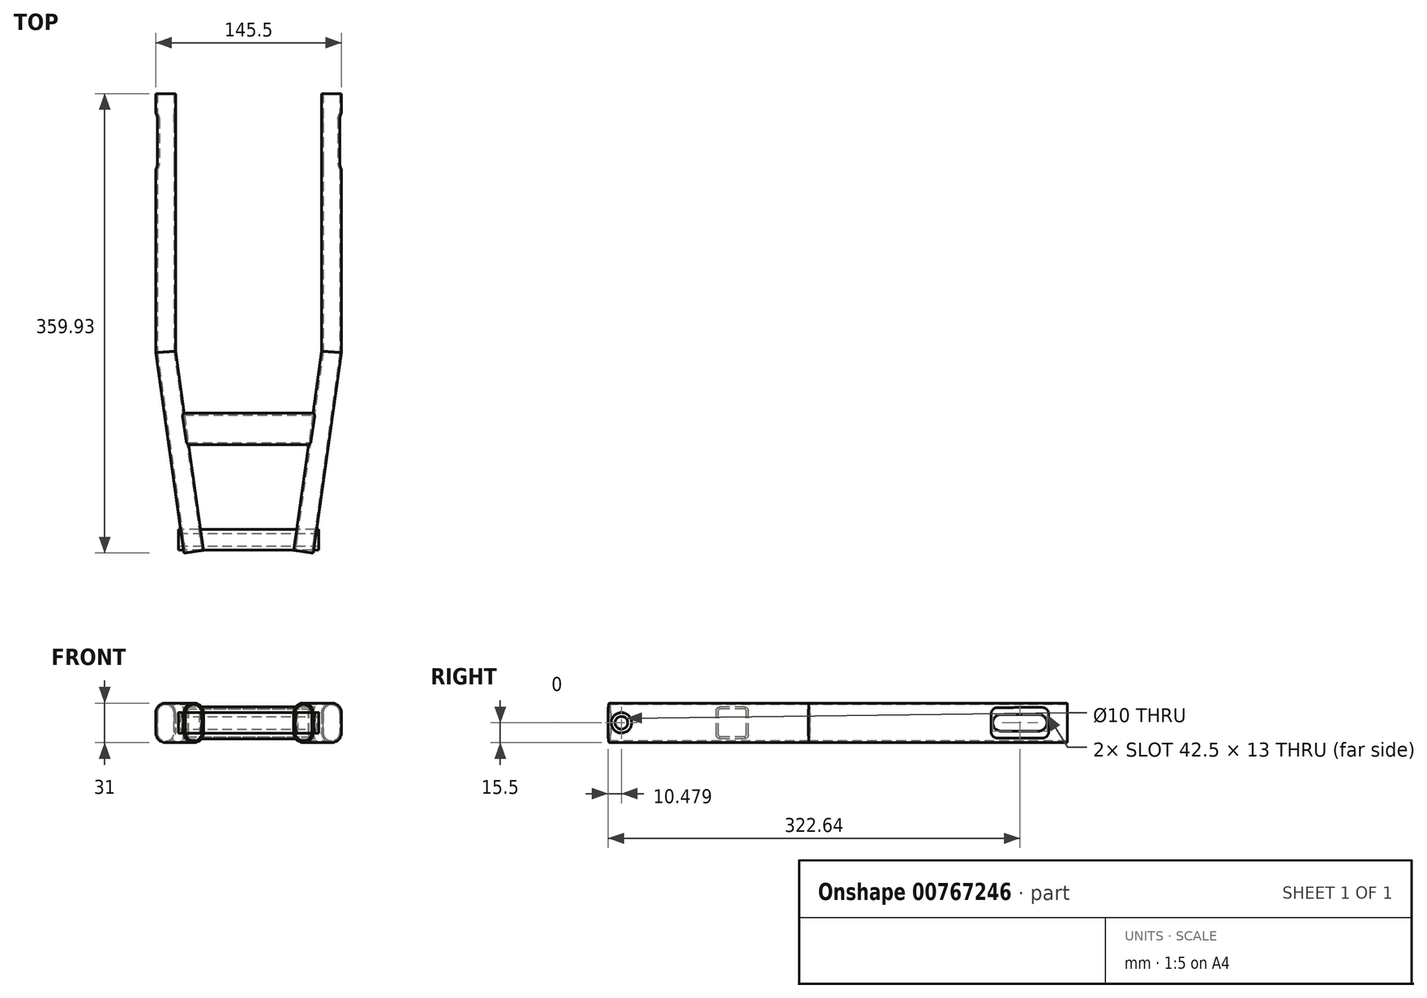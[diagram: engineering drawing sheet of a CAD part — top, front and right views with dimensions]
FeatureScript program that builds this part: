
annotation { "Feature Type Name" : "Feature", "Feature Type Description" : "" }
export const myFeature = defineFeature(function(context is Context, id is Id, definition is map)
    precondition{}
    {
        {
            var Q0;
            Q0=qCreatedBy(makeId("Top.planeOp"),FACE);
            var sketch = newSketch(context, id + "F0", { "sketchPlane" : qUnion([Q0])});
            skLineSegment(sketch, "E0", {"start": v(-65, 0) * mm, "end": v(-65, -202.36) * mm});
            skLineSegment(sketch, "E1", {"start": v(-65, -202.36) * mm, "end": v(-43, -358.85) * mm});
            skSolve(sketch);
        }
        {
            var Q0;
            Q0=qCreatedBy(makeId("Front.planeOp"),FACE);
            var sketch = newSketch(context, id + "F1", { "sketchPlane" : qUnion([Q0])});
            skLineSegment(sketch, "E2.left", {"start": v(-72.75, 7.75) * mm, "end": v(-72.75, -7.75) * mm});
            skLineSegment(sketch, "E2.right", {"start": v(-57.25, 7.75) * mm, "end": v(-57.25, -7.75) * mm});
            skPoint(sketch, "E2.middle", {"position": v(-65, 0) * mm});
            skArc(sketch, "E3", {"start": v(-57.25, 7.75) * mm, "mid": v(-65, 15.5) * mm, "end": v(-72.75, 7.75) * mm});
            skArc(sketch, "E4", {"start": v(-57.25, -7.75) * mm, "mid": v(-65, -15.5) * mm, "end": v(-72.75, -7.75) * mm});
            skPoint(sketch, "E5.left.start.orphan", {"position": v(-71.55, 6.63) * mm});
            skPoint(sketch, "E5.top.start.orphan", {"position": v(-71.55, -6.63) * mm});
            skPoint(sketch, "E5.right.end.orphan", {"position": v(-58.45, -6.63) * mm});
            skPoint(sketch, "E5.right.start.orphan", {"position": v(-58.45, 6.63) * mm});
            skArc(sketch, "E6.0", {"start": v(-58.45, 7.75) * mm, "mid": v(-65, 14.3) * mm, "end": v(-71.55, 7.75) * mm});
            skLineSegment(sketch, "E6.1", {"start": v(-58.45, 7.75) * mm, "end": v(-58.45, -7.75) * mm});
            skArc(sketch, "E6.2", {"start": v(-58.45, -7.75) * mm, "mid": v(-65, -14.3) * mm, "end": v(-71.55, -7.75) * mm});
            skLineSegment(sketch, "E6.3", {"start": v(-71.55, 7.75) * mm, "end": v(-71.55, -7.75) * mm});
            skSolve(sketch);
        }
        {
            var Q0;
            Q0=makeQuery(id+"F1.imprint","IMPRINT",FACE,{"disambiguationData":[TD([[makeQuery(id+"F1.imprint","IMPRINT",EDGE,{"derivedFrom":sQuery(id+"F1.wireOp",EDGE,"E2.left")}),1.0]])]});
            var Q1;
            Q1=sQuery(id+"F0.wireOp",EDGE,"E0");
            var Q2;
            Q2=sQuery(id+"F0.wireOp",EDGE,"E1");
            sweep(context, id + "F2", {"profiles" : qUnion([Q0]), "path" : qUnion([Q1, Q2])});
        }
        {
            var Q0;
            Q0=makeQuery(id+"F2.opSweep","SWEPT_BODY",BODY,{"disambiguationData":[OSD([sQuery(id+"F0.wireOp",EDGE,"E1"),sQuery(id+"F1.wireOp",EDGE,"E2.left"),sQuery(id+"F1.wireOp",EDGE,"E2.right"),sQuery(id+"F1.wireOp",EDGE,"E3"),sQuery(id+"F1.wireOp",EDGE,"E4"),sQuery(id+"F1.wireOp",EDGE,"E6.0"),sQuery(id+"F1.wireOp",EDGE,"E6.1"),sQuery(id+"F1.wireOp",EDGE,"E6.2"),sQuery(id+"F1.wireOp",EDGE,"E6.3")])]});
            var Q1;
            Q1=qCreatedBy(makeId("Right.planeOp"),FACE);
            mirror(context, id + "F3", {"entities" : qUnion([Q0]), "mirrorPlane" : qUnion([Q1])});
        }
        {
            var Q0;
            Q0=qCreatedBy(makeId("Right.planeOp"),FACE);
            var sketch = newSketch(context, id + "F4", { "sketchPlane" : qUnion([Q0])});
            skLineSegment(sketch, "E7.bottom", {"start": v(-52.04, 6.5) * mm, "end": v(-22.54, 6.5) * mm});
            skLineSegment(sketch, "E7.top", {"start": v(-52.04, -6.5) * mm, "end": v(-22.54, -6.5) * mm});
            skLineSegment(sketch, "E7.left", {"start": v(-52.04, 6.5) * mm, "end": v(-52.04, -6.5) * mm});
            skLineSegment(sketch, "E7.right", {"start": v(-22.54, 6.5) * mm, "end": v(-22.54, -6.5) * mm});
            skPoint(sketch, "E7.middle", {"position": v(-37.3, 0) * mm});
            skArc(sketch, "E8", {"start": v(-22.54, 6.5) * mm, "mid": v(-16.04, 0) * mm, "end": v(-22.54, -6.5) * mm});
            skArc(sketch, "E9", {"start": v(-52.04, 6.5) * mm, "mid": v(-58.54, 0) * mm, "end": v(-52.04, -6.5) * mm});
            skSolve(sketch);
        }
        {
            var Q0;
            Q0 = qSketchRegion(id + "F4", true);
            extrude(context, id + "F5", {"entities" : qUnion([Q0]), "operationType" : NewBodyOperationType.REMOVE, "endBound" : BoundingType.SYMMETRIC, "oppositeDirection" : true, "depth" : 1000 * mm, "offsetDistance" : 25 * mm});
        }
        {
            var Q0;
            Q0=makeQuery(id+"F2.opSweep","SWEPT_FACE",FACE,{"disambiguationData":[OSD([sQuery(id+"F0.wireOp",EDGE,"E0"),sQuery(id+"F1.wireOp",EDGE,"E2.left")])]});
            var sketch = newSketch(context, id + "F6", { "sketchPlane" : qUnion([Q0])});
            skPoint(sketch, "E10.middle", {"position": v(37.3, 0) * mm});
            skPoint(sketch, "E10.middle.positionSnap0", {"position": v(37.3, 6.5) * mm});
            skPoint(sketch, "E10.centerSnap0", {"position": v(37.3, 6.5) * mm});
            skArc(sketch, "E11", {"start": v(54.79, 12) * mm, "mid": v(58.33, 10.54) * mm, "end": v(59.79, 7) * mm});
            skArc(sketch, "E12", {"start": v(59.79, -7) * mm, "mid": v(58.33, -10.54) * mm, "end": v(54.79, -12) * mm});
            skArc(sketch, "E13", {"start": v(19.8, -12.03) * mm, "mid": v(16.23, -10.56) * mm, "end": v(14.76, -7) * mm});
            skArc(sketch, "E14", {"start": v(19.79, 12.03) * mm, "mid": v(16.23, 10.56) * mm, "end": v(14.76, 7) * mm});
            skLineSegment(sketch, "E15", {"start": v(14.76, 7) * mm, "end": v(14.76, -7) * mm});
            skLineSegment(sketch, "E16", {"start": v(19.8, -12.03) * mm, "end": v(54.79, -12) * mm});
            skLineSegment(sketch, "E17", {"start": v(59.79, -7) * mm, "end": v(59.79, 7) * mm});
            skLineSegment(sketch, "E18", {"start": v(54.79, 12) * mm, "end": v(19.79, 12.03) * mm});
            skSolve(sketch);
        }
        {
            var Q0;
            Q0 = qSketchRegion(id + "F6", true);
            extrude(context, id + "F7", {"entities" : qUnion([Q0]), "operationType" : NewBodyOperationType.REMOVE, "oppositeDirection" : true, "depth" : 4 * mm, "offsetDistance" : 25 * mm});
        }
        {
            var Q0;
            Q0=makeQuery(id+"F3.opPattern","COPY",BODY,{"derivedFrom":makeQuery(id+"F2.opSweep","SWEPT_BODY",BODY,{"disambiguationData":[OSD([sQuery(id+"F0.wireOp",EDGE,"E1"),sQuery(id+"F1.wireOp",EDGE,"E2.left"),sQuery(id+"F1.wireOp",EDGE,"E2.right"),sQuery(id+"F1.wireOp",EDGE,"E3"),sQuery(id+"F1.wireOp",EDGE,"E4"),sQuery(id+"F1.wireOp",EDGE,"E6.0"),sQuery(id+"F1.wireOp",EDGE,"E6.1"),sQuery(id+"F1.wireOp",EDGE,"E6.2"),sQuery(id+"F1.wireOp",EDGE,"E6.3")])]}),"instanceName":"1"});
            deleteBodies(context, id + "F8", {"entities" : qUnion([Q0])});
        }
        {
            var Q0;
            Q0=makeQuery(id+"F2.opSweep","SWEPT_BODY",BODY,{"disambiguationData":[OSD([sQuery(id+"F0.wireOp",EDGE,"E1"),sQuery(id+"F1.wireOp",EDGE,"E2.left"),sQuery(id+"F1.wireOp",EDGE,"E2.right"),sQuery(id+"F1.wireOp",EDGE,"E3"),sQuery(id+"F1.wireOp",EDGE,"E4"),sQuery(id+"F1.wireOp",EDGE,"E6.0"),sQuery(id+"F1.wireOp",EDGE,"E6.1"),sQuery(id+"F1.wireOp",EDGE,"E6.2"),sQuery(id+"F1.wireOp",EDGE,"E6.3")])]});
            var Q1;
            Q1=qCreatedBy(makeId("Right.planeOp"),FACE);
            mirror(context, id + "F9", {"entities" : qUnion([Q0]), "mirrorPlane" : qUnion([Q1])});
        }
        {
            var Q0;
            Q0=qCreatedBy(makeId("Right.planeOp"),FACE);
            var sketch = newSketch(context, id + "F10", { "sketchPlane" : qUnion([Q0])});
            skCircle(sketch, "E19", {"center": v(-349.45, 0) * mm, "radius": 8 * mm});
            skCircle(sketch, "E20", {"center": v(-349.45, 0) * mm, "radius": 5 * mm});
            skSolve(sketch);
        }
        {
            var Q0;
            Q0=qCreatedBy(makeId("Right.planeOp"),FACE);
            var sketch = newSketch(context, id + "F11", { "sketchPlane" : qUnion([Q0])});
            skLineSegment(sketch, "E21.bottom", {"start": v(-250.12, 12.5) * mm, "end": v(-275.12, 12.5) * mm});
            skLineSegment(sketch, "E21.top", {"start": v(-250.12, -12.5) * mm, "end": v(-275.12, -12.5) * mm});
            skLineSegment(sketch, "E21.left", {"start": v(-250.12, 12.5) * mm, "end": v(-250.12, -12.5) * mm});
            skLineSegment(sketch, "E21.right", {"start": v(-275.12, 12.5) * mm, "end": v(-275.12, -12.5) * mm});
            skPoint(sketch, "E21.middle", {"position": v(-262.62, 0) * mm});
            skLineSegment(sketch, "E22.bottom", {"start": v(-251.72, 10.9) * mm, "end": v(-273.52, 10.9) * mm});
            skLineSegment(sketch, "E22.top", {"start": v(-251.72, -10.9) * mm, "end": v(-273.52, -10.9) * mm});
            skLineSegment(sketch, "E22.left", {"start": v(-251.72, 10.9) * mm, "end": v(-251.72, -10.9) * mm});
            skLineSegment(sketch, "E22.right", {"start": v(-273.52, 10.9) * mm, "end": v(-273.52, -10.9) * mm});
            skSolve(sketch);
        }
        {
            var Q0;
            Q0 = qSketchRegion(id + "F11", true);
            var Q1;
            Q1=makeQuery(id+"F2.opSweep","SWEPT_BODY",BODY,{"disambiguationData":[OSD([sQuery(id+"F0.wireOp",EDGE,"E1"),sQuery(id+"F1.wireOp",EDGE,"E2.left"),sQuery(id+"F1.wireOp",EDGE,"E2.right"),sQuery(id+"F1.wireOp",EDGE,"E3"),sQuery(id+"F1.wireOp",EDGE,"E4"),sQuery(id+"F1.wireOp",EDGE,"E6.0"),sQuery(id+"F1.wireOp",EDGE,"E6.1"),sQuery(id+"F1.wireOp",EDGE,"E6.2"),sQuery(id+"F1.wireOp",EDGE,"E6.3")])]});
            extrude(context, id + "F12", {"entities" : qUnion([Q0]), "operationType" : NewBodyOperationType.ADD, "endBound" : BoundingType.UP_TO_BODY, "oppositeDirection" : true, "depth" : 25 * mm, "endBoundEntityBody" : qUnion([Q1]), "offsetDistance" : 25 * mm});
        }
        {
            var Q0;
            Q0=makeQuery(id+"F12.opExtrude","SWEPT_EDGE",EDGE,{"disambiguationData":[OSD([sQuery(id+"F11.wireOp",EDGE,"E22.top"),sQuery(id+"F11.wireOp",EDGE,"E22.left")])]});
            var Q1;
            Q1=makeQuery(id+"F12.opExtrude","SWEPT_EDGE",EDGE,{"disambiguationData":[OSD([sQuery(id+"F11.wireOp",EDGE,"E22.top"),sQuery(id+"F11.wireOp",EDGE,"E22.right")])]});
            var Q2;
            Q2=makeQuery(id+"F12.opExtrude","SWEPT_EDGE",EDGE,{"disambiguationData":[OSD([sQuery(id+"F11.wireOp",EDGE,"E22.bottom"),sQuery(id+"F11.wireOp",EDGE,"E22.right")])]});
            var Q3;
            Q3=makeQuery(id+"F12.opExtrude","SWEPT_EDGE",EDGE,{"disambiguationData":[OSD([sQuery(id+"F11.wireOp",EDGE,"E22.bottom"),sQuery(id+"F11.wireOp",EDGE,"E22.left")])]});
            fillet(context, id + "F13", {"entities" : qUnion([Q0, Q1, Q2, Q3]), "radius" : 1.4 * mm, "tangentPropagation" : true, "allowEdgeOverflow" : false});
        }
        {
            var Q0;
            Q0=makeQuery(id+"F12.opExtrude","SWEPT_EDGE",EDGE,{"disambiguationData":[OSD([sQuery(id+"F11.wireOp",EDGE,"E21.bottom"),sQuery(id+"F11.wireOp",EDGE,"E21.left")])]});
            var Q1;
            Q1=makeQuery(id+"F12.opExtrude","SWEPT_EDGE",EDGE,{"disambiguationData":[OSD([sQuery(id+"F11.wireOp",EDGE,"E21.bottom"),sQuery(id+"F11.wireOp",EDGE,"E21.right")])]});
            var Q2;
            Q2=makeQuery(id+"F12.opExtrude","SWEPT_EDGE",EDGE,{"disambiguationData":[OSD([sQuery(id+"F11.wireOp",EDGE,"E21.top"),sQuery(id+"F11.wireOp",EDGE,"E21.right")])]});
            var Q3;
            Q3=makeQuery(id+"F12.opExtrude","SWEPT_EDGE",EDGE,{"disambiguationData":[OSD([sQuery(id+"F11.wireOp",EDGE,"E21.top"),sQuery(id+"F11.wireOp",EDGE,"E21.left")])]});
            fillet(context, id + "F14", {"entities" : qUnion([Q0, Q1, Q2, Q3]), "radius" : 3 * mm, "tangentPropagation" : true, "allowEdgeOverflow" : false});
        }
        {
            var Q0;
            Q0=makeQuery(id+"F2.opSweep","SWEPT_BODY",BODY,{"disambiguationData":[OSD([sQuery(id+"F0.wireOp",EDGE,"E1"),sQuery(id+"F1.wireOp",EDGE,"E2.left"),sQuery(id+"F1.wireOp",EDGE,"E2.right"),sQuery(id+"F1.wireOp",EDGE,"E3"),sQuery(id+"F1.wireOp",EDGE,"E4"),sQuery(id+"F1.wireOp",EDGE,"E6.0"),sQuery(id+"F1.wireOp",EDGE,"E6.1"),sQuery(id+"F1.wireOp",EDGE,"E6.2"),sQuery(id+"F1.wireOp",EDGE,"E6.3")])]});
            var Q1;
            Q1=qCreatedBy(makeId("Right.planeOp"),FACE);
            mirror(context, id + "F15", {"entities" : qUnion([Q0]), "mirrorPlane" : qUnion([Q1])});
        }
        {
            var Q0;
            Q0=makeQuery(id+"F10.imprint","IMPRINT",FACE,{"disambiguationData":[TD([[makeQuery(id+"F10.imprint","IMPRINT",EDGE,{"derivedFrom":sQuery(id+"F10.wireOp",EDGE,"E19")}),1.0]])]});
            var Q1;
            Q1=makeQuery(id+"F10.imprint","IMPRINT",FACE,{"disambiguationData":[TD([[makeQuery(id+"F10.imprint","IMPRINT",EDGE,{"derivedFrom":sQuery(id+"F10.wireOp",EDGE,"E20")}),1.0]])]});
            extrude(context, id + "F16", {"entities" : qUnion([Q0, Q1]), "operationType" : NewBodyOperationType.ADD, "endBound" : BoundingType.SYMMETRIC, "depth" : 110 * mm, "offsetDistance" : 25 * mm});
        }
        {
            var Q0;
            Q0=makeQuery(id+"F16.opExtrude","CAP_FACE",FACE,{"disambiguationData":[OSD([sQuery(id+"F10.wireOp",EDGE,"E19")])],"isStart":false});
            var sketch = newSketch(context, id + "F17", { "sketchPlane" : qUnion([Q0])});
            skCircle(sketch, "E23", {"center": v(-349.45, 0) * mm, "radius": 5 * mm});
            skSolve(sketch);
        }
        {
            var Q0;
            Q0 = qSketchRegion(id + "F17", true);
            extrude(context, id + "F18", {"entities" : qUnion([Q0]), "operationType" : NewBodyOperationType.REMOVE, "oppositeDirection" : true, "depth" : 110 * mm, "offsetDistance" : 25 * mm});
        }
    });
